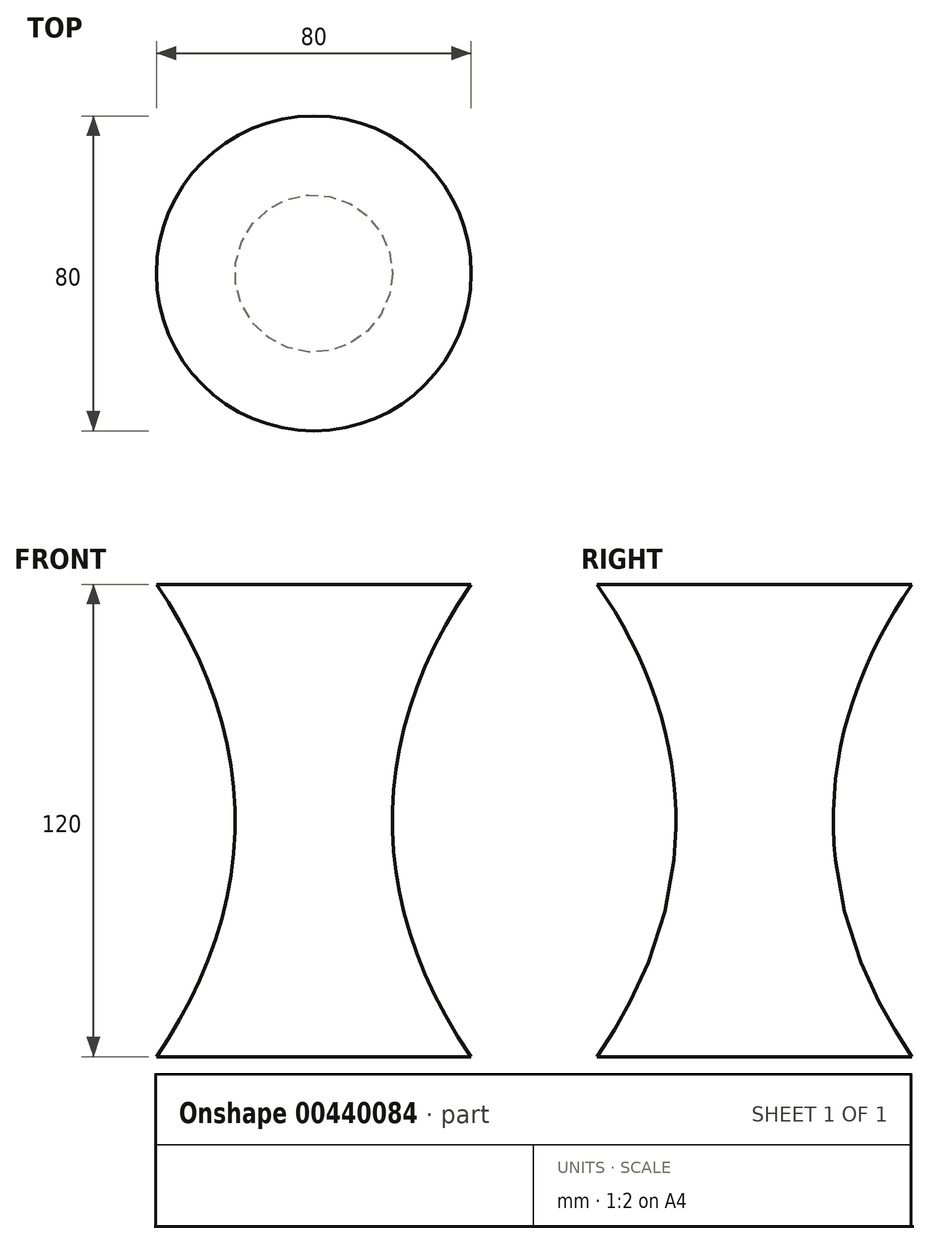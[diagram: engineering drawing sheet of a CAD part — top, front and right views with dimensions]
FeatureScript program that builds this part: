
annotation { "Feature Type Name" : "Feature", "Feature Type Description" : "" }
export const myFeature = defineFeature(function(context is Context, id is Id, definition is map)
    precondition{}
    {
        {
            var Q0;
            Q0=qCreatedBy(makeId("Front.planeOp"),FACE);
            var sketch = newSketch(context, id + "F0", { "sketchPlane" : qUnion([Q0])});
            skPoint(sketch, "E0", {"position": v(40, 60) * mm});
            skPoint(sketch, "E1", {"position": v(20, 0) * mm});
            skPoint(sketch, "E2", {"position": v(40, -60) * mm});
            skLineSegment(sketch, "E3", {"start": v(0, 56.72) * mm, "end": v(0, -56.68) * mm});
            skFitSpline(sketch, "E4", {"points": [v(40, 60) * mm, v(20, 0) * mm, v(40, -60) * mm], "startDerivative": vector(-82.67, -120) * mm, "endDerivative": vector(82.67, -120) * mm});
            skLineSegment(sketch, "E5", {"start": v(40, 60) * mm, "end": v(0, 60) * mm});
            skLineSegment(sketch, "E6", {"start": v(0, 60) * mm, "end": v(0, -60) * mm});
            skLineSegment(sketch, "E7", {"start": v(0, -60) * mm, "end": v(40, -60) * mm});
            skSolve(sketch);
        }
        {
            var Q0;
            Q0 = qSketchRegion(id + "F0", true);
            var Q1;
            Q1=sQuery(id+"F0.wireOp",EDGE,"E6");
            revolve(context, id + "F1", {"entities" : qUnion([Q0]), "axis" : qUnion([Q1]), "revolveType" : RevolveType.FULL});
        }
    });
